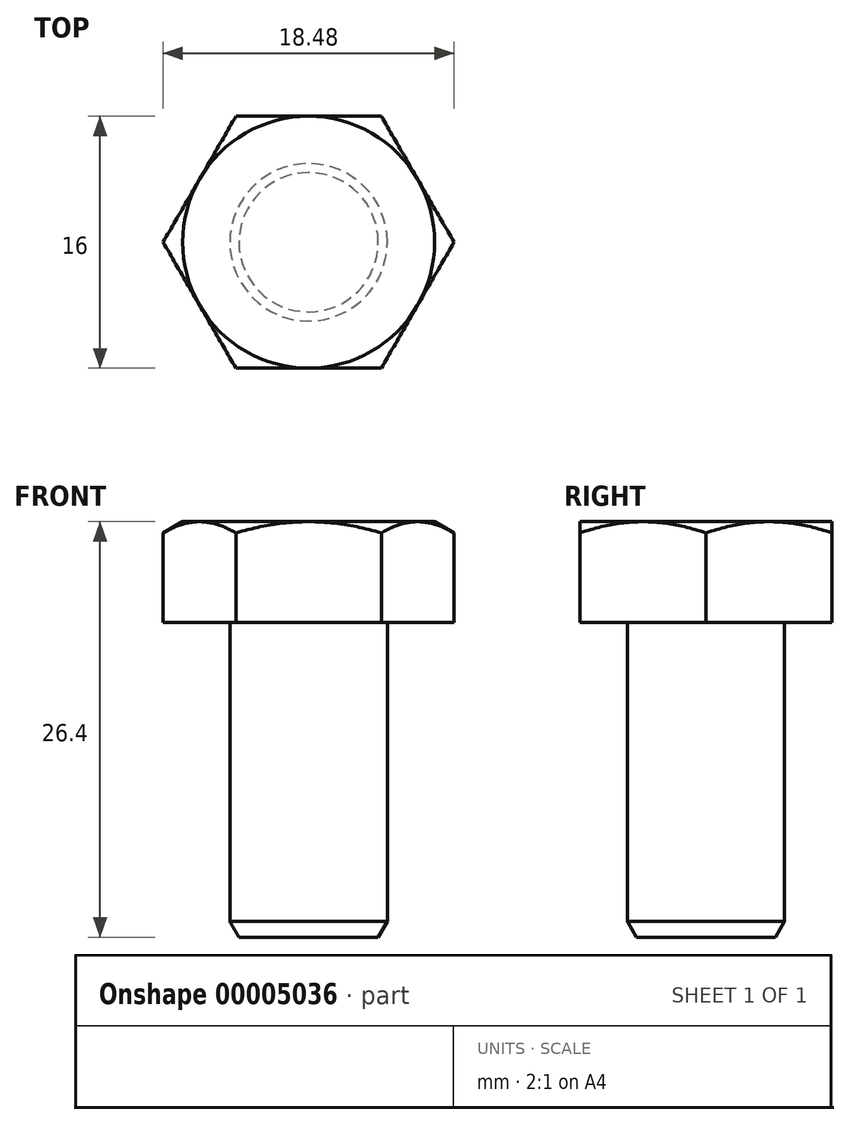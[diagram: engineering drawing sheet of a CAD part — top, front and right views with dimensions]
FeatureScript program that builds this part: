
annotation { "Feature Type Name" : "Feature", "Feature Type Description" : "" }
export const myFeature = defineFeature(function(context is Context, id is Id, definition is map)
    precondition{}
    {
        {
            var Q0;
            Q0=qCreatedBy(makeId("Front.planeOp"),FACE);
            var sketch = newSketch(context, id + "F0", { "sketchPlane" : qUnion([Q0])});
            skLineSegment(sketch, "E0", {"start": v(20.77, 6.19) * mm, "end": v(20.77, -0.21) * mm});
            skLineSegment(sketch, "E1", {"start": v(20.77, -0.21) * mm, "end": v(30.77, -0.21) * mm});
            skLineSegment(sketch, "E2", {"start": v(30.77, -0.21) * mm, "end": v(30.77, 5.03) * mm});
            skLineSegment(sketch, "E3", {"start": v(30.77, 5.03) * mm, "end": v(28.77, 6.19) * mm});
            skLineSegment(sketch, "E4", {"start": v(28.77, 6.19) * mm, "end": v(20.77, 6.19) * mm});
            skSolve(sketch);
        }
        {
            var Q0;
            Q0 = qSketchRegion(id + "F0", true);
            var Q1;
            Q1=sQuery(id+"F0.wireOp",EDGE,"E0");
            revolve(context, id + "F1", {"entities" : qUnion([Q0]), "axis" : qUnion([Q1]), "revolveType" : RevolveType.FULL});
        }
        {
            var Q0;
            Q0=makeQuery(id+"F1.opRevolve","SWEPT_FACE",FACE,{"disambiguationData":[OSD([sQuery(id+"F0.wireOp",EDGE,"E4")])]});
            var sketch = newSketch(context, id + "F2", { "sketchPlane" : qUnion([Q0])});
            skCircle(sketch, "E5.cCircle", {"center": v(20.77, 0) * mm, "radius": 8 * mm, "construction": true});
            skLineSegment(sketch, "E5.0", {"start": v(16.15, 8) * mm, "end": v(25.4, 8) * mm});
            skLineSegment(sketch, "E5.1", {"start": v(25.4, 8) * mm, "end": v(30, 0) * mm});
            skLineSegment(sketch, "E5.2", {"start": v(30, 0) * mm, "end": v(25.4, -8) * mm});
            skLineSegment(sketch, "E5.3", {"start": v(25.4, -8) * mm, "end": v(16.15, -8) * mm});
            skLineSegment(sketch, "E5.4", {"start": v(16.15, -8) * mm, "end": v(11.53, 0) * mm});
            skLineSegment(sketch, "E5.5", {"start": v(11.53, 0) * mm, "end": v(16.15, 8) * mm});
            skPoint(sketch, "E5.0.midPoint", {"position": v(20.77, 8) * mm});
            skSolve(sketch);
        }
        {
            var Q0;
            Q0 = qSketchRegion(id + "F2", true);
            extrude(context, id + "F3", {"entities" : qUnion([Q0]), "operationType" : NewBodyOperationType.INTERSECT, "oppositeDirection" : true, "depth" : 25 * mm});
        }
        {
            var Q0;
            Q0=makeQuery(id+"F1.opRevolve","SWEPT_FACE",FACE,{"disambiguationData":[OSD([sQuery(id+"F0.wireOp",EDGE,"E1")])]});
            var sketch = newSketch(context, id + "F4", { "sketchPlane" : qUnion([Q0])});
            skPoint(sketch, "E6", {"position": v(20.77, 8) * mm});
            skCircle(sketch, "E7", {"center": v(20.77, 0) * mm, "radius": 5 * mm});
            skSolve(sketch);
        }
        {
            var Q0;
            Q0 = qSketchRegion(id + "F4", true);
            extrude(context, id + "F5", {"entities" : qUnion([Q0]), "operationType" : NewBodyOperationType.ADD, "depth" : 20 * mm});
        }
        {
            var Q0;
            Q0=makeQuery(id+"F5.opExtrude","CAP_EDGE",EDGE,{"disambiguationData":[OSD([sQuery(id+"F4.wireOp",EDGE,"E7")])],"isStart":false});
            chamfer(context, id + "F6", {"entities" : qUnion([Q0]), "chamferType" : ChamferType.OFFSET_ANGLE, "width" : 1 * mm, "oppositeDirection" : true, "angle" : 30 * degree, "tangentPropagation" : true});
        }
    });
